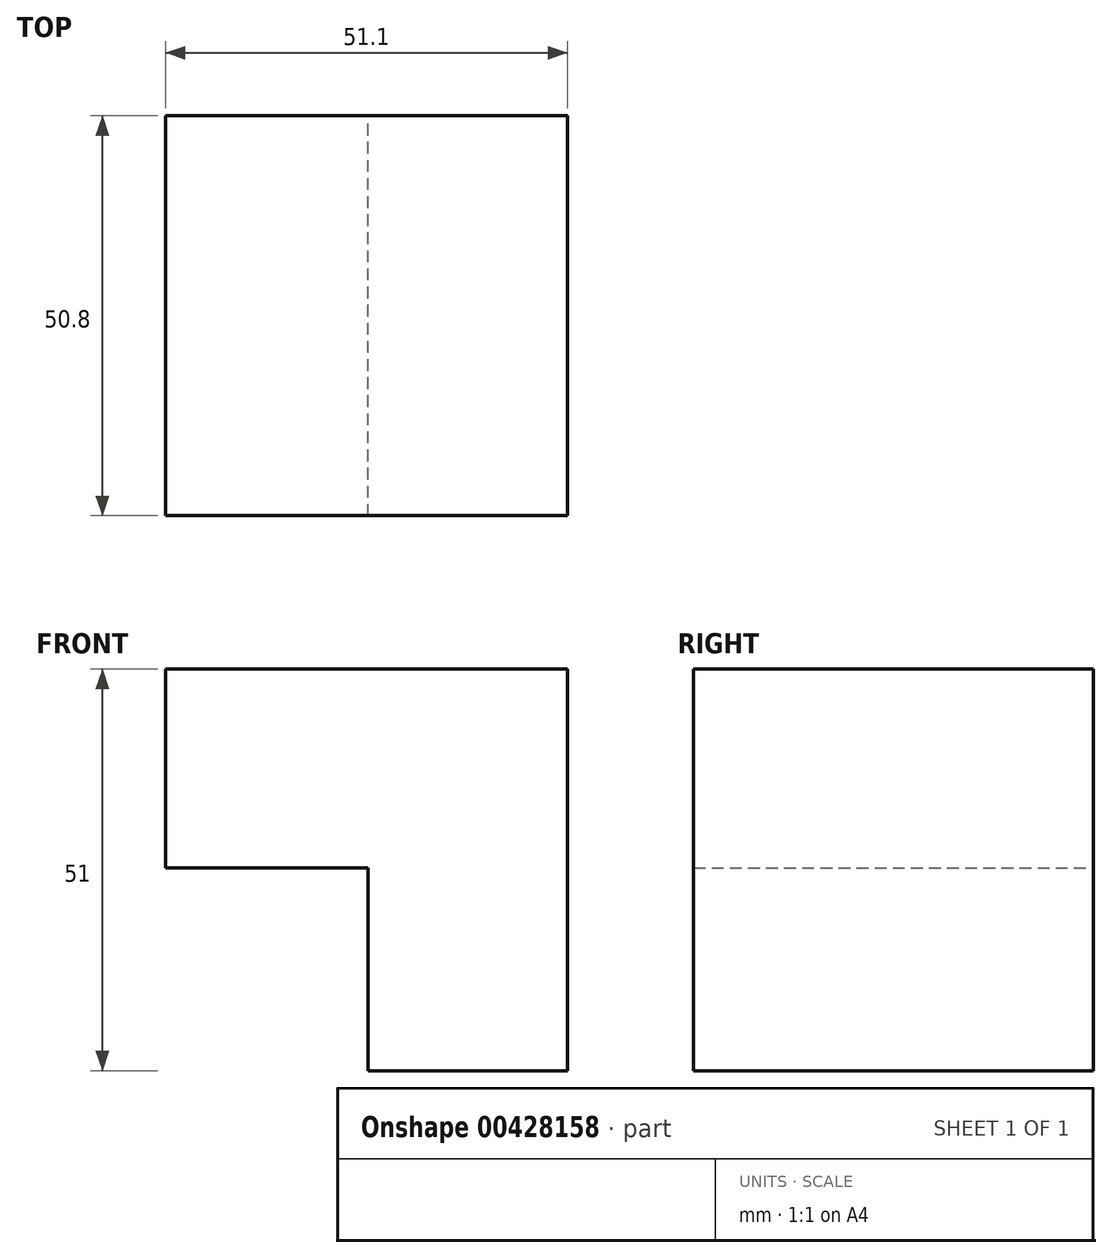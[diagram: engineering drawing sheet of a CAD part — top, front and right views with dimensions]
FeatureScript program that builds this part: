
annotation { "Feature Type Name" : "Feature", "Feature Type Description" : "" }
export const myFeature = defineFeature(function(context is Context, id is Id, definition is map)
    precondition{}
    {
        {
            var Q0;
            Q0=qCreatedBy(makeId("Front.planeOp"),FACE);
            var sketch = newSketch(context, id + "F0", { "sketchPlane" : qUnion([Q0])});
            skLineSegment(sketch, "E0", {"start": v(0, 0) * mm, "end": v(-51.1, 0) * mm});
            skLineSegment(sketch, "E1", {"start": v(-51.1, 0) * mm, "end": v(-51.1, -25.26) * mm});
            skLineSegment(sketch, "E2", {"start": v(-51.1, -25.26) * mm, "end": v(-25.36, -25.26) * mm});
            skLineSegment(sketch, "E3", {"start": v(-25.36, -25.26) * mm, "end": v(-25.36, -51) * mm});
            skLineSegment(sketch, "E4", {"start": v(-25.36, -51) * mm, "end": v(0, -51) * mm});
            skLineSegment(sketch, "E5", {"start": v(0, -51) * mm, "end": v(0, 0) * mm});
            skSolve(sketch);
        }
        {
            var Q0;
            Q0=makeQuery(id+"F0.imprint","IMPRINT",FACE,{"disambiguationData":[TD([[makeQuery(id+"F0.imprint","IMPRINT",EDGE,{"derivedFrom":sQuery(id+"F0.wireOp",EDGE,"E0")}),1.0]])]});
            extrude(context, id + "F1", {"entities" : qUnion([Q0]), "depth" : 50.8 * mm});
        }
    });
